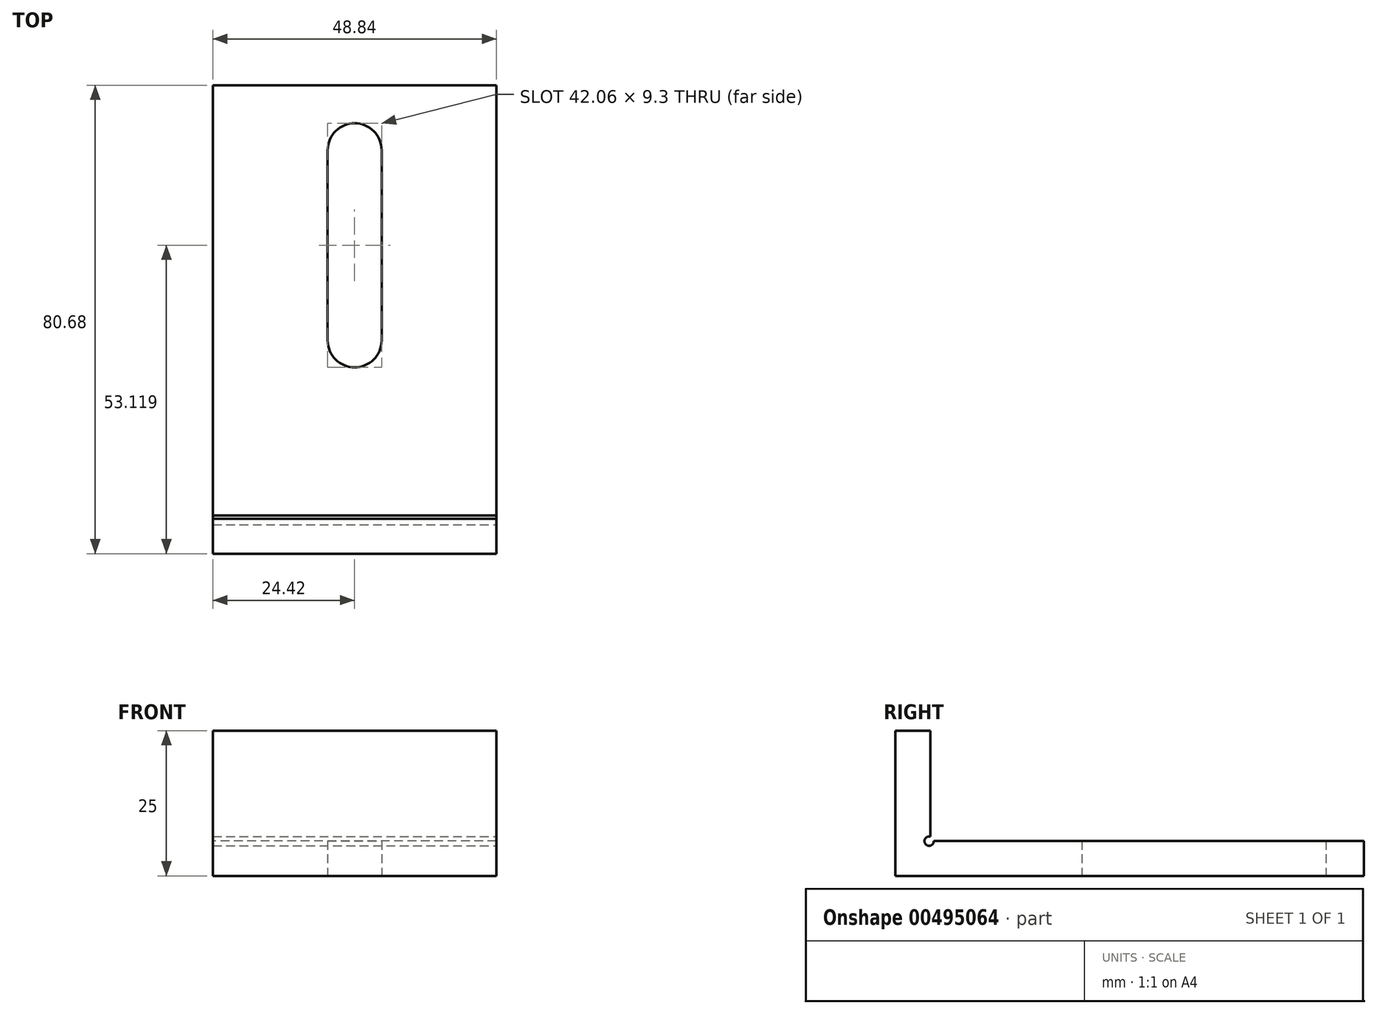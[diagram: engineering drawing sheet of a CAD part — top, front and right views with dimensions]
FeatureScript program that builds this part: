
annotation { "Feature Type Name" : "Feature", "Feature Type Description" : "" }
export const myFeature = defineFeature(function(context is Context, id is Id, definition is map)
    precondition{}
    {
        {
            var Q0;
            Q0=qCreatedBy(makeId("Top.planeOp"),FACE);
            var sketch = newSketch(context, id + "F0", { "sketchPlane" : qUnion([Q0])});
            skLineSegment(sketch, "E0.bottom", {"start": v(24.42, -40.34) * mm, "end": v(-24.42, -40.34) * mm});
            skLineSegment(sketch, "E0.top", {"start": v(24.42, 40.34) * mm, "end": v(-24.42, 40.34) * mm});
            skLineSegment(sketch, "E0.left", {"start": v(24.42, -40.34) * mm, "end": v(24.42, 40.34) * mm});
            skLineSegment(sketch, "E0.right", {"start": v(-24.42, -40.34) * mm, "end": v(-24.42, 40.34) * mm});
            skPoint(sketch, "E0.middle", {"position": v(0, 0) * mm});
            skLineSegment(sketch, "E1", {"start": v(-24.42, -34.34) * mm, "end": v(24.42, -34.34) * mm});
            skLineSegment(sketch, "E2", {"start": v(0, -3.6) * mm, "end": v(0, 29.16) * mm});
            skPoint(sketch, "E2.startSnap0", {"position": v(0, -34.34) * mm});
            skArc(sketch, "E3.0.startCap", {"start": v(4.65, -3.6) * mm, "mid": v(0, -8.25) * mm, "end": v(-4.65, -3.6) * mm});
            skArc(sketch, "E3.0.endCap", {"start": v(-4.65, 29.16) * mm, "mid": v(0, 33.81) * mm, "end": v(4.65, 29.16) * mm});
            skLineSegment(sketch, "E3.0.left", {"start": v(-4.65, -3.6) * mm, "end": v(-4.65, 29.16) * mm});
            skLineSegment(sketch, "E3.0.right", {"start": v(4.65, -3.6) * mm, "end": v(4.65, 29.16) * mm});
            skSolve(sketch);
        }
        {
            var Q0;
            {var subQ0=sQuery(id+"F0.wireOp",EDGE,"E0.bottom");Q0=makeQuery(id+"F0.imprint","IMPRINT",FACE,{"disambiguationData":[TD([[makeQuery(id+"F0.imprint","IMPRINT",EDGE,{"derivedFrom":subQ0}),-1.0]])]});}
            extrude(context, id + "F1", {"entities" : qUnion([Q0]), "depth" : 25 * mm});
        }
        {
            var Q0;
            Q0 = qSketchRegion(id + "F0", true);
            extrude(context, id + "F2", {"entities" : qUnion([Q0]), "operationType" : NewBodyOperationType.ADD, "depth" : 6 * mm});
        }
        {
            var Q0;
            Q0=qCreatedBy(makeId("Right.planeOp"),FACE);
            var sketch = newSketch(context, id + "F3", { "sketchPlane" : qUnion([Q0])});
            skCircle(sketch, "E4", {"center": v(-34.53, 5.98) * mm, "radius": 0.8 * mm});
            skPoint(sketch, "E4.first.point", {"position": v(-33.75, 5.8) * mm});
            skPoint(sketch, "E4.second.point", {"position": v(-35.3, 6.18) * mm});
            skPoint(sketch, "E4.third.point", {"position": v(-35.02, 5.34) * mm});
            skSolve(sketch);
        }
        {
            var Q0;
            Q0=makeQuery(id+"F3.imprint","IMPRINT",FACE,{"disambiguationData":[TD([[makeQuery(id+"F3.imprint","IMPRINT",EDGE,{"derivedFrom":sQuery(id+"F3.wireOp",EDGE,"E4")}),1.0]])]});
            extrude(context, id + "F4", {"entities" : qUnion([Q0]), "operationType" : NewBodyOperationType.REMOVE, "endBound" : BoundingType.SYMMETRIC, "oppositeDirection" : true, "depth" : 50.5 * mm});
        }
    });
